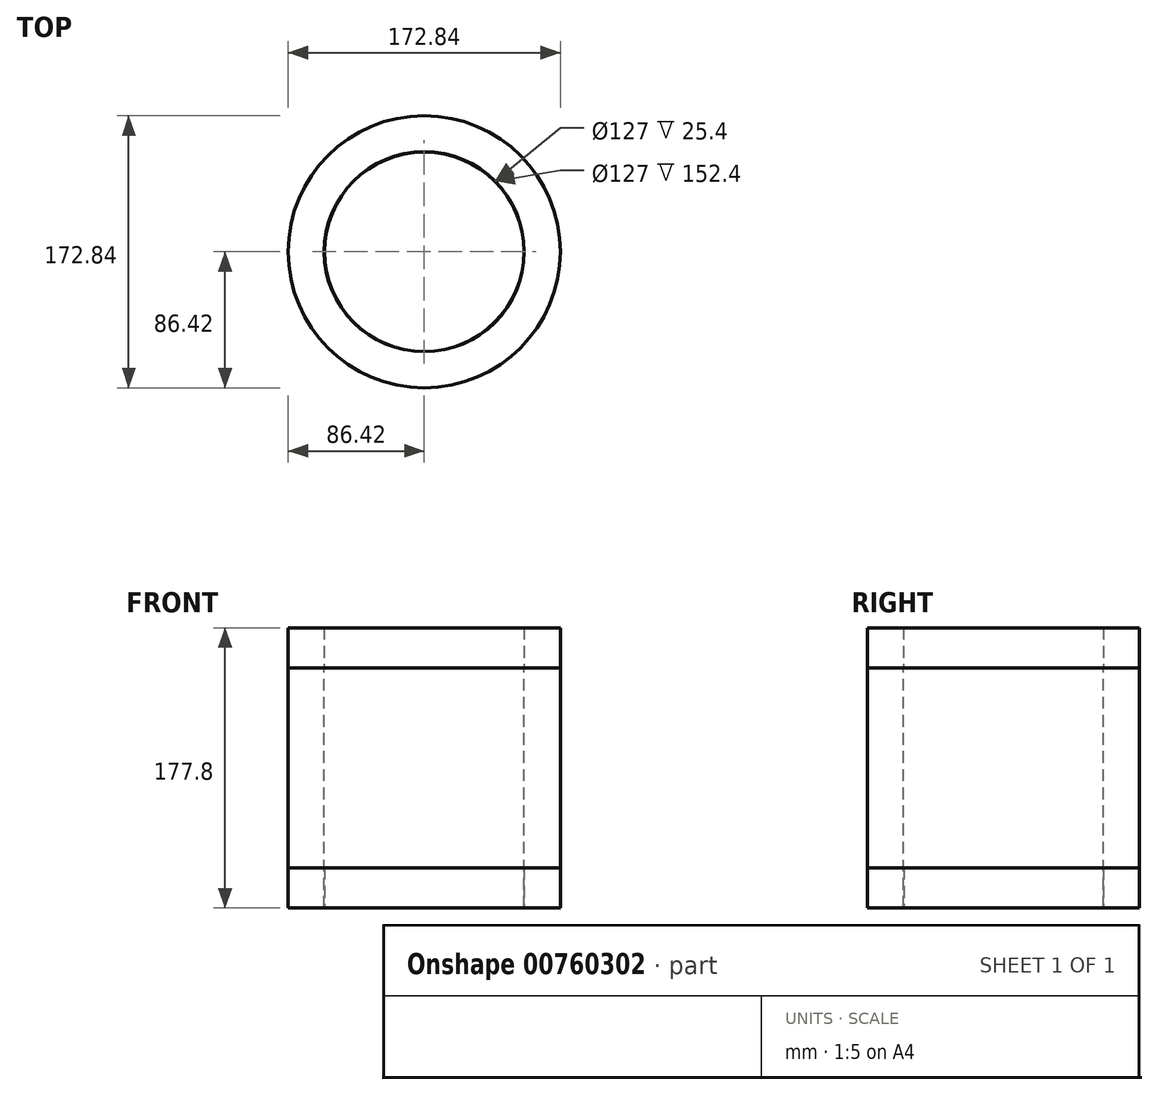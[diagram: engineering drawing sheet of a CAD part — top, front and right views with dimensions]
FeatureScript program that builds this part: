
annotation { "Feature Type Name" : "Feature", "Feature Type Description" : "" }
export const myFeature = defineFeature(function(context is Context, id is Id, definition is map)
    precondition{}
    {
        {
            var Q0;
            Q0=qCreatedBy(makeId("Top.planeOp"),FACE);
            var sketch = newSketch(context, id + "F0", { "sketchPlane" : qUnion([Q0])});
            skCircle(sketch, "E0", {"center": v(0, 0) * mm, "radius": 86.42 * mm});
            skSolve(sketch);
        }
        {
            var Q0;
            Q0=qSketchRegion(id+"F0",true);
            extrude(context, id + "F1", {"entities" : qUnion([Q0]), "depth" : 152.4 * mm, "offsetDistance" : 25.4 * mm});
        }
        {
            var Q0;
            Q0=makeQuery(id+"F1.opExtrude","CAP_FACE",FACE,{"disambiguationData":[OSD([sQuery(id+"F0.wireOp",EDGE,"E0")])],"isStart":false});
            var sketch = newSketch(context, id + "F2", { "sketchPlane" : qUnion([Q0])});
            skCircle(sketch, "E1", {"center": v(0, 0) * mm, "radius": 69.9 * mm});
            skSolve(sketch);
        }
        {
            var Q0;
            Q0=sQuery(id+"F2.wireOp",VERTEX,"E1.center");
            var Q1;
            Q1=makeQuery(id+"F1.opExtrude","SWEPT_BODY",BODY,{"disambiguationData":[OSD([sQuery(id+"F0.wireOp",EDGE,"E0")])]});
            hole(context, id + "F3", {"style" : HoleStyle.SIMPLE, "endStyle" : HoleEndStyle.THROUGH, "holeDiameter" : 127 * mm, "majorDiameter" : 6.35 * mm, "isTappedThrough" : true, "tappedDepth" : 12.7 * mm, "tapClearance" : 3, "locations" : qUnion([Q0]), "scope" : qUnion([Q1])});
        }
        {
            var Q0;
            Q0=qCreatedBy(makeId("Top.planeOp"),FACE);
            var sketch = newSketch(context, id + "F4", { "sketchPlane" : qUnion([Q0])});
            skCircle(sketch, "E2", {"center": v(0, 0) * mm, "radius": 62.88 * mm});
            skCircle(sketch, "E3", {"center": v(0, 0) * mm, "radius": 67.7 * mm});
            skSolve(sketch);
        }
        {
            var Q0;
            Q0=sQuery(id+"F4.wireOp",EDGE,"E3");
            extrude(context, id + "F5", {"bodyType" : ToolBodyType.SURFACE, "surfaceEntities" : qUnion([Q0]), "depth" : 19.05 * mm, "offsetDistance" : 25.4 * mm});
        }
        {
            var Q0;
            Q0=qCreatedBy(makeId("Top.planeOp"),FACE);
            var sketch = newSketch(context, id + "F6", { "sketchPlane" : qUnion([Q0])});
            skCircle(sketch, "E4", {"center": v(0, 0) * mm, "radius": 63.34 * mm});
            skCircle(sketch, "E5", {"center": v(0, 0) * mm, "radius": 64.1 * mm});
            skSolve(sketch);
        }
        {
            var Q0;
            Q0=makeQuery(id+"F6.imprint","IMPRINT",FACE,{"disambiguationData":[TD([[makeQuery(id+"F6.imprint","IMPRINT",EDGE,{"derivedFrom":sQuery(id+"F6.wireOp",EDGE,"E4")}),1.0]])]});
            var Q1;
            Q1=makeQuery(id+"F1.opExtrude","CAP_FACE",FACE,{"disambiguationData":[OSD([sQuery(id+"F0.wireOp",EDGE,"E0")])],"isStart":false});
            var Q2;
            Q2=qSketchRegion(id+"F0",true);
            var Q3;
            Q3=sQuery(id+"F6.wireOp",EDGE,"E5");
            var Q4;
            Q4=sQuery(id+"F6.wireOp",EDGE,"E4");
            extrude(context, id + "F7", {"entities" : qUnion([Q0, Q1, Q2]), "surfaceEntities" : qUnion([Q3, Q4]), "depth" : 25.4 * mm, "offsetDistance" : 25.4 * mm});
        }
    });
